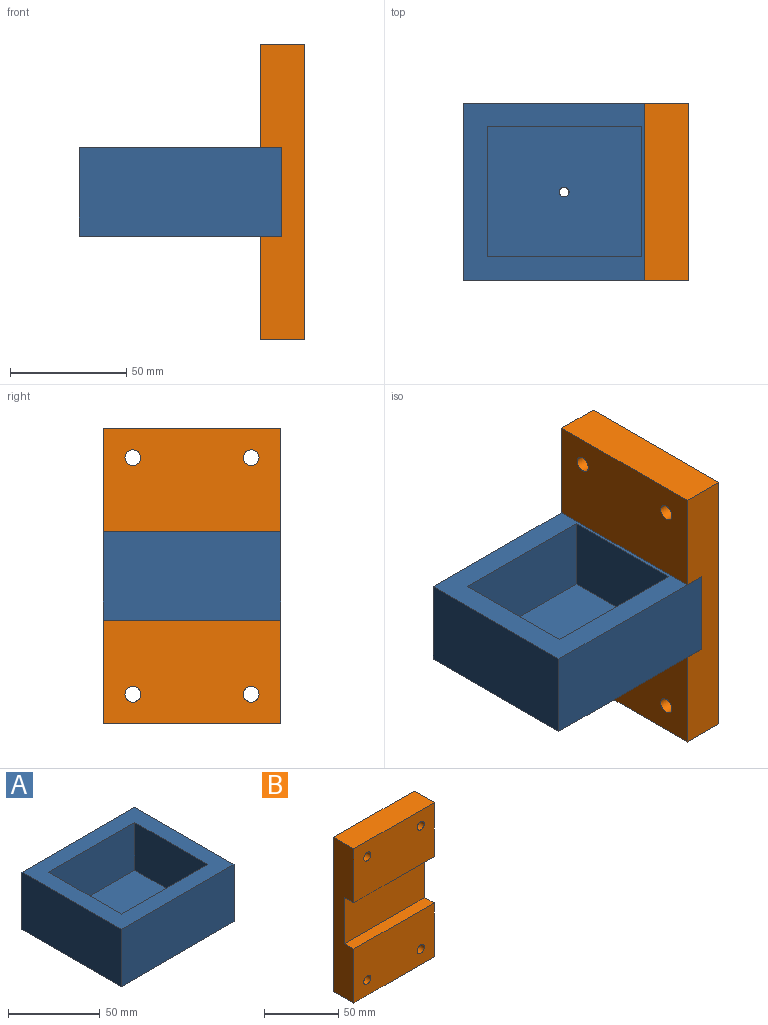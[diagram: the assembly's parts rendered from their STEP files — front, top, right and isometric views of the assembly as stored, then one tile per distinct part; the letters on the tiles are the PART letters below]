
ASSEMBLY  parts=2 mates=1
PART A: 12 faces, bbox 86.8x76.2x38.1 mm
  f0: plane 86.75x76.2mm, normal (0,0,1), area 2907.6mm2, adj f2,f3,f4,f5,f6,f7,f8,f9
  f1: plane 86.75x76.2mm, normal (0,0,-1), area 6596.6mm2, adj f2,f3,f4,f5,f11
  f2: plane 76.2x38.01mm, normal (1,0,0), area 2896.5mm2, adj f0,f1,f4,f5
  f3: plane 76.2x38.1mm, normal (-1,0,0), area 2903.2mm2, adj f0,f1,f4,f5
  f4: plane 86.75x38.1mm, normal (0,1,0), area 3301.4mm2, adj f0,f1,f2,f3
  f5: plane 86.75x38.1mm, normal (0,-1,0), area 3301.4mm2, adj f0,f1,f2,f3
  f6: plane 66.3x31.82mm, normal (0,-1,0), area 2103.9mm2, adj f0,f7,f9,f10
  f7: plane 55.88x31.75mm, normal (1,0,0), area 1774.2mm2, adj f0,f6,f8,f10
  f8: plane 66.3x31.82mm, normal (0,1,0), area 2103.9mm2, adj f0,f7,f9,f10
  f9: plane 55.88x31.75mm, normal (-1,0,0), area 1774.2mm2, adj f0,f6,f8,f10
  f10: plane 66.26x55.88mm, normal (0,0,1), area 3689mm2, adj f6,f7,f8,f9,f11
  f11: cylinder r=2.1mm len=6.31mm, axis (0,0,-1), area 83mm2, adj f1,f10
PART B: 14 faces, bbox 76.2x19.1x127 mm
  f0: plane 76.2x44.41mm, normal (0,-1,0), area 3312.5mm2, adj f1,f2,f3,f8,f11,f12
  f1: plane 127x19.05mm, normal (-1,0,0), area 2084.8mm2, adj f0,f2,f4,f5,f6,f7,f8,f9
  f2: plane 76.2x19.05mm, normal (0,0,-1), area 1451.6mm2, adj f0,f1,f3,f6
  f3: plane 127x19.05mm, normal (1,0,0), area 2084.8mm2, adj f0,f2,f4,f5,f6,f7,f8,f9
  f4: plane 76.2x19.05mm, normal (0,0,1), area 1451.6mm2, adj f1,f3,f5,f6
  f5: plane 76.2x44.41mm, normal (0,-1,0), area 3312.5mm2, adj f1,f3,f4,f7,f10,f13
  f6: plane 127x76.2mm, normal (0,1,0), area 9534mm2, adj f1,f2,f3,f4,f10,f11,f12,f13
  f7: plane 76.2x8.76mm, normal (0,0,-1), area 667.7mm2, adj f1,f3,f5,f9
  f8: plane 76.2x8.76mm, normal (0,0,1), area 667.7mm2, adj f0,f1,f3,f9
  f9: plane 76.2x38.18mm, normal (0,-1,0), area 2909mm2, adj f1,f3,f7,f8
  f10: cylinder r=3.38mm len=19.05mm, axis (0,-1,0), area 404.4mm2, adj f5,f6
  f11: cylinder r=3.38mm len=19.05mm, axis (0,-1,0), area 404.4mm2, adj f0,f6
  f12: cylinder r=3.38mm len=19.05mm, axis (0,-1,0), area 404.4mm2, adj f0,f6
  f13: cylinder r=3.38mm len=19.05mm, axis (0,-1,0), area 404.4mm2, adj f5,f6
PLACE A t=(0.32,0,-0.28)mm
PLACE B rot(axis=(0.71,0.71,0),180deg) t=(44.4,0,4.99)mm
MATE parallel B.f9 <-> A.f2  axis (-1,0,0) through (43.64,0,4.99)mm
